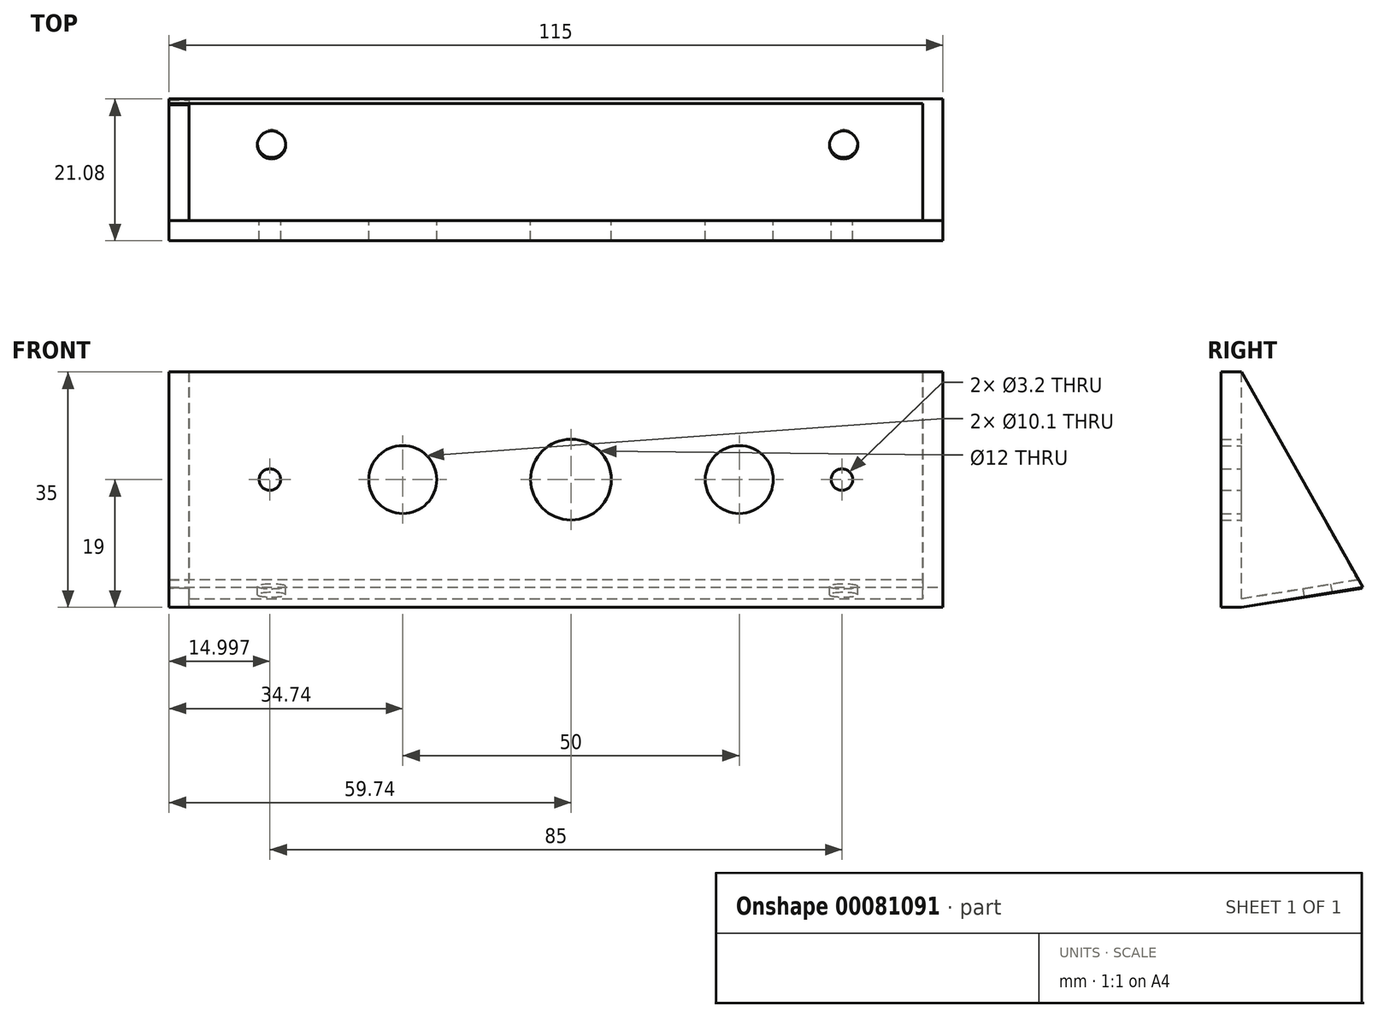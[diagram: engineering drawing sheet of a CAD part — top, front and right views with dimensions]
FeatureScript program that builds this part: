
annotation { "Feature Type Name" : "Feature", "Feature Type Description" : "" }
export const myFeature = defineFeature(function(context is Context, id is Id, definition is map)
    precondition{}
    {
        {
            var Q0;
            Q0=qCreatedBy(makeId("Front.planeOp"),FACE);
            var sketch = newSketch(context, id + "F0", { "sketchPlane" : qUnion([Q0])});
            skLineSegment(sketch, "E0.bottom", {"start": v(55.26, 0) * mm, "end": v(-59.74, 0) * mm});
            skLineSegment(sketch, "E0.top", {"start": v(55.26, 35) * mm, "end": v(-59.74, 35) * mm});
            skLineSegment(sketch, "E0.left", {"start": v(55.26, 0) * mm, "end": v(55.26, 35) * mm});
            skLineSegment(sketch, "E0.right", {"start": v(-59.74, 0) * mm, "end": v(-59.74, 35) * mm});
            skCircle(sketch, "E1", {"center": v(-44.74, 19) * mm, "radius": 1.6 * mm});
            skCircle(sketch, "E2.1.0.0", {"center": v(40.26, 19) * mm, "radius": 1.6 * mm});
            skLineSegment(sketch, "E2.direction1", {"start": v(-44.74, 19) * mm, "end": v(40.26, 19) * mm, "construction": true});
            skCircle(sketch, "E3", {"center": v(25, 19) * mm, "radius": 5.05 * mm});
            skCircle(sketch, "E4", {"center": v(-25, 19) * mm, "radius": 5.05 * mm});
            skCircle(sketch, "E5", {"center": v(0, 19) * mm, "radius": 6 * mm});
            skPoint(sketch, "E5.centerSnap0", {"position": v(-2.24, 19) * mm});
            skSolve(sketch);
        }
        {
            var Q0;
            Q0 = qSketchRegion(id + "F0", true);
            var Q1;
            Q1=makeQuery(id+"F0.imprint","IMPRINT",FACE,{"disambiguationData":[TD([[makeQuery(id+"F0.imprint","IMPRINT",EDGE,{"derivedFrom":sQuery(id+"F0.wireOp",EDGE,"E0.bottom")}),-1.0]])]});
            extrude(context, id + "F1", {"entities" : qUnion([Q0, Q1]), "depth" : 3 * mm});
        }
        {
            var Q0;
            Q0=makeQuery(id+"F1.opExtrude","SWEPT_FACE",FACE,{"disambiguationData":[OSD([sQuery(id+"F0.wireOp",EDGE,"E0.right")])]});
            var sketch = newSketch(context, id + "F2", { "sketchPlane" : qUnion([Q0])});
            skLineSegment(sketch, "E6", {"start": v(0, 35) * mm, "end": v(-17.95, 2.82) * mm});
            skLineSegment(sketch, "E7", {"start": v(-17.95, 2.82) * mm, "end": v(0, 0) * mm});
            skSolve(sketch);
        }
        {
            var Q0;
            Q0 = qSketchRegion(id + "F2", true);
            var Q1;
            Q1=makeQuery(id+"F2.imprint","IMPRINT",FACE,{"disambiguationData":[TD([[makeQuery(id+"F2.imprint","IMPRINT",EDGE,{"derivedFrom":sQuery(id+"F2.wireOp",EDGE,"E6")}),1.0]])]});
            extrude(context, id + "F3", {"entities" : qUnion([Q0, Q1]), "operationType" : NewBodyOperationType.ADD, "oppositeDirection" : true, "depth" : 3 * mm});
        }
        {
            var Q0;
            Q0=makeQuery(id+"F1.opExtrude","SWEPT_FACE",FACE,{"disambiguationData":[OSD([sQuery(id+"F0.wireOp",EDGE,"E0.left")])]});
            var sketch = newSketch(context, id + "F4", { "sketchPlane" : qUnion([Q0])});
            skLineSegment(sketch, "E8", {"start": v(0, 35) * mm, "end": v(18.08, 2.98) * mm});
            skLineSegment(sketch, "E9", {"start": v(18.08, 2.98) * mm, "end": v(0, 0) * mm});
            skSolve(sketch);
        }
        {
            var Q0;
            Q0 = qSketchRegion(id + "F4", true);
            var Q1;
            Q1=makeQuery(id+"F4.imprint","IMPRINT",FACE,{"disambiguationData":[TD([[makeQuery(id+"F4.imprint","IMPRINT",EDGE,{"derivedFrom":sQuery(id+"F4.wireOp",EDGE,"E8")}),-1.0]])]});
            extrude(context, id + "F5", {"entities" : qUnion([Q0, Q1]), "operationType" : NewBodyOperationType.ADD, "oppositeDirection" : true, "depth" : 3 * mm});
        }
        {
            var Q0;
            Q0=makeQuery(id+"F5.opExtrude","CAP_FACE",FACE,{"disambiguationData":[OSD([sQuery(id+"F0.wireOp",EDGE,"E0.left"),sQuery(id+"F4.wireOp",EDGE,"E8"),sQuery(id+"F4.wireOp",EDGE,"E9")])],"isStart":false});
            var sketch = newSketch(context, id + "F6", { "sketchPlane" : qUnion([Q0])});
            skLineSegment(sketch, "E10", {"start": v(-18.08, 2.98) * mm, "end": v(-17.42, 4.15) * mm});
            skLineSegment(sketch, "E11", {"start": v(-17.42, 4.15) * mm, "end": v(0, 1.28) * mm});
            skSolve(sketch);
        }
        {
            var Q0;
            Q0 = qSketchRegion(id + "F6", true);
            var Q1;
            Q1=makeQuery(id+"F6.imprint","IMPRINT",FACE,{"disambiguationData":[TD([[makeQuery(id+"F6.imprint","IMPRINT",EDGE,{"derivedFrom":sQuery(id+"F6.wireOp",EDGE,"E10")}),1.0]])]});
            extrude(context, id + "F7", {"entities" : qUnion([Q0, Q1]), "operationType" : NewBodyOperationType.ADD, "depth" : 112 * mm});
        }
        {
            var Q0;
            Q0=makeQuery(id+"F7.opExtrude","SWEPT_FACE",FACE,{"disambiguationData":[OSD([sQuery(id+"F6.wireOp",EDGE,"E11")])]});
            var sketch = newSketch(context, id + "F8", { "sketchPlane" : qUnion([Q0])});
            skCircle(sketch, "E12", {"center": v(40.5, 11.6) * mm, "radius": 2.1 * mm});
            skCircle(sketch, "E13.1.0.0", {"center": v(-44.5, 11.6) * mm, "radius": 2.1 * mm});
            skLineSegment(sketch, "E13.direction1", {"start": v(40.5, 11.6) * mm, "end": v(-44.5, 11.6) * mm, "construction": true});
            skSolve(sketch);
        }
        {
            var Q0;
            Q0 = qSketchRegion(id + "F8", true);
            extrude(context, id + "F9", {"entities" : qUnion([Q0]), "operationType" : NewBodyOperationType.REMOVE, "endBound" : BoundingType.THROUGH_ALL, "oppositeDirection" : true, "depth" : 25 * mm});
        }
    });
